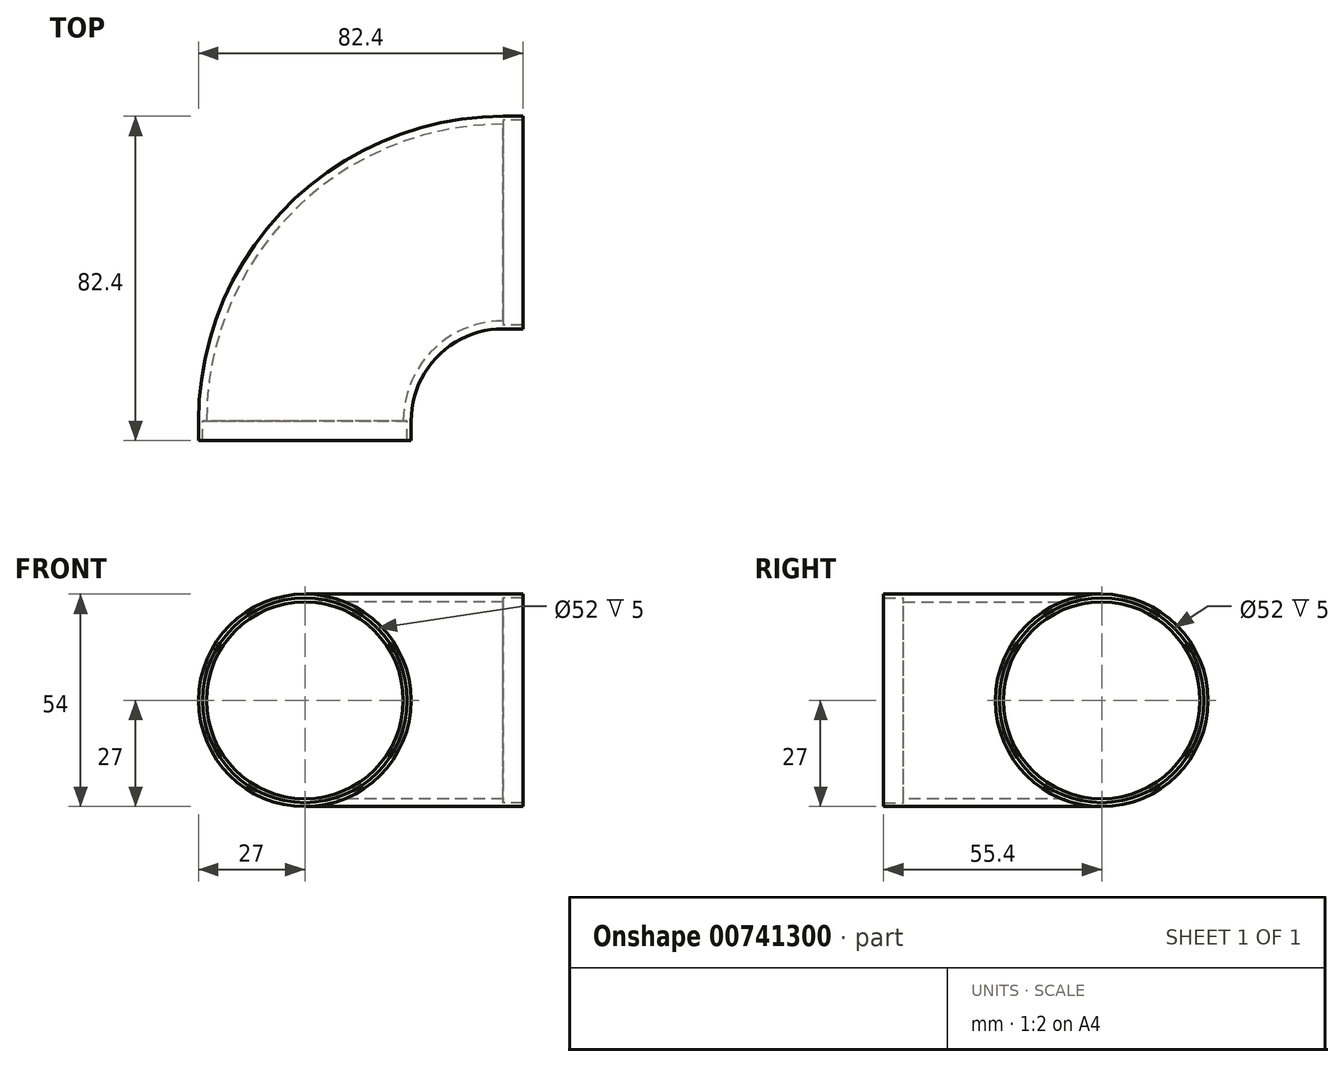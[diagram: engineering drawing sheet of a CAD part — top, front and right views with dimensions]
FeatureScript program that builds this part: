
annotation { "Feature Type Name" : "Feature", "Feature Type Description" : "" }
export const myFeature = defineFeature(function(context is Context, id is Id, definition is map)
    precondition{}
    {
        {
            var Q0;
            Q0=qCreatedBy(makeId("Front.planeOp"),FACE);
            var sketch = newSketch(context, id + "F0", { "sketchPlane" : qUnion([Q0])});
            skCircle(sketch, "E0", {"center": v(0, 0) * mm, "radius": 27 * mm});
            skCircle(sketch, "E1", {"center": v(0, 0) * mm, "radius": 25 * mm});
            skLineSegment(sketch, "E2", {"start": v(50.4, 43.13) * mm, "end": v(50.4, -62.12) * mm, "construction": true});
            skSolve(sketch);
        }
        {
            var Q0;
            Q0=makeQuery(id+"F0.imprint","IMPRINT",FACE,{"disambiguationData":[TD([[makeQuery(id+"F0.imprint","IMPRINT",EDGE,{"derivedFrom":sQuery(id+"F0.wireOp",EDGE,"E0")}),1.0]])]});
            var Q1;
            Q1=sQuery(id+"F0.wireOp",EDGE,"E2");
            revolve(context, id + "F1", {"surfaceOperationType" : NewSurfaceOperationType.NEW, "entities" : qUnion([Q0]), "axis" : qUnion([Q1]), "revolveType" : RevolveType.ONE_DIRECTION, "angle" : 90 * degree});
        }
        {
            var Q0;
            Q0=qCreatedBy(makeId("Front.planeOp"),FACE);
            var sketch = newSketch(context, id + "F2", { "sketchPlane" : qUnion([Q0])});
            skCircle(sketch, "E3", {"center": v(0, 0) * mm, "radius": 27 * mm});
            skCircle(sketch, "E4", {"center": v(0, 0) * mm, "radius": 26 * mm});
            skSolve(sketch);
        }
        {
            var Q0;
            Q0=qSketchRegion(id+"F2",true);
            extrude(context, id + "F3", {"entities" : qUnion([Q0]), "operationType" : NewBodyOperationType.ADD, "depth" : 5 * mm, "offsetDistance" : 25 * mm});
        }
        {
            var Q0;
            Q0=makeQuery(id+"F1.opRevolve","CAP_FACE",FACE,{"disambiguationData":[OSD([sQuery(id+"F0.wireOp",EDGE,"E0"),sQuery(id+"F0.wireOp",EDGE,"E1")])],"isStart":false});
            var sketch = newSketch(context, id + "F4", { "sketchPlane" : qUnion([Q0])});
            skCircle(sketch, "E5", {"center": v(50.4, 0) * mm, "radius": 26 * mm});
            skCircle(sketch, "E6", {"center": v(50.4, 0) * mm, "radius": 27 * mm});
            skSolve(sketch);
        }
        {
            var Q0;
            Q0=qSketchRegion(id+"F4",true);
            extrude(context, id + "F5", {"entities" : qUnion([Q0]), "operationType" : NewBodyOperationType.ADD, "depth" : 5 * mm, "offsetDistance" : 25 * mm});
        }
    });
